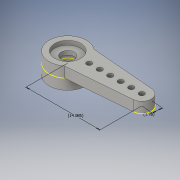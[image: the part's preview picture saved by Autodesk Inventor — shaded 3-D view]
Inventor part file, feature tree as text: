
AUTODESK INVENTOR PART (.ipt)
format: ipt  version: 2016 (Build 200138000, 138)  size: 162,816 bytes
history: native  units: in
note: dims shown in document units (in); Inventor stores cm internally (conversion verified against a paired STEP export)
features: other x3, sketch x1
ambient origin geometry x8: Origin, YZ Plane, XZ Plane, XY Plane, X Axis, Y Axis, Z Axis, Center Point
bodies: Solid1 (feature_tree)
feature tree (4):
  other  "SG90 plastic Horn.ipt"
  other  "Solid1::SG90 plastic Horn.ipt"
  other  "TaggingFeature1"
  sketch  "Sketch1"  dims[d0=0.3937in]
